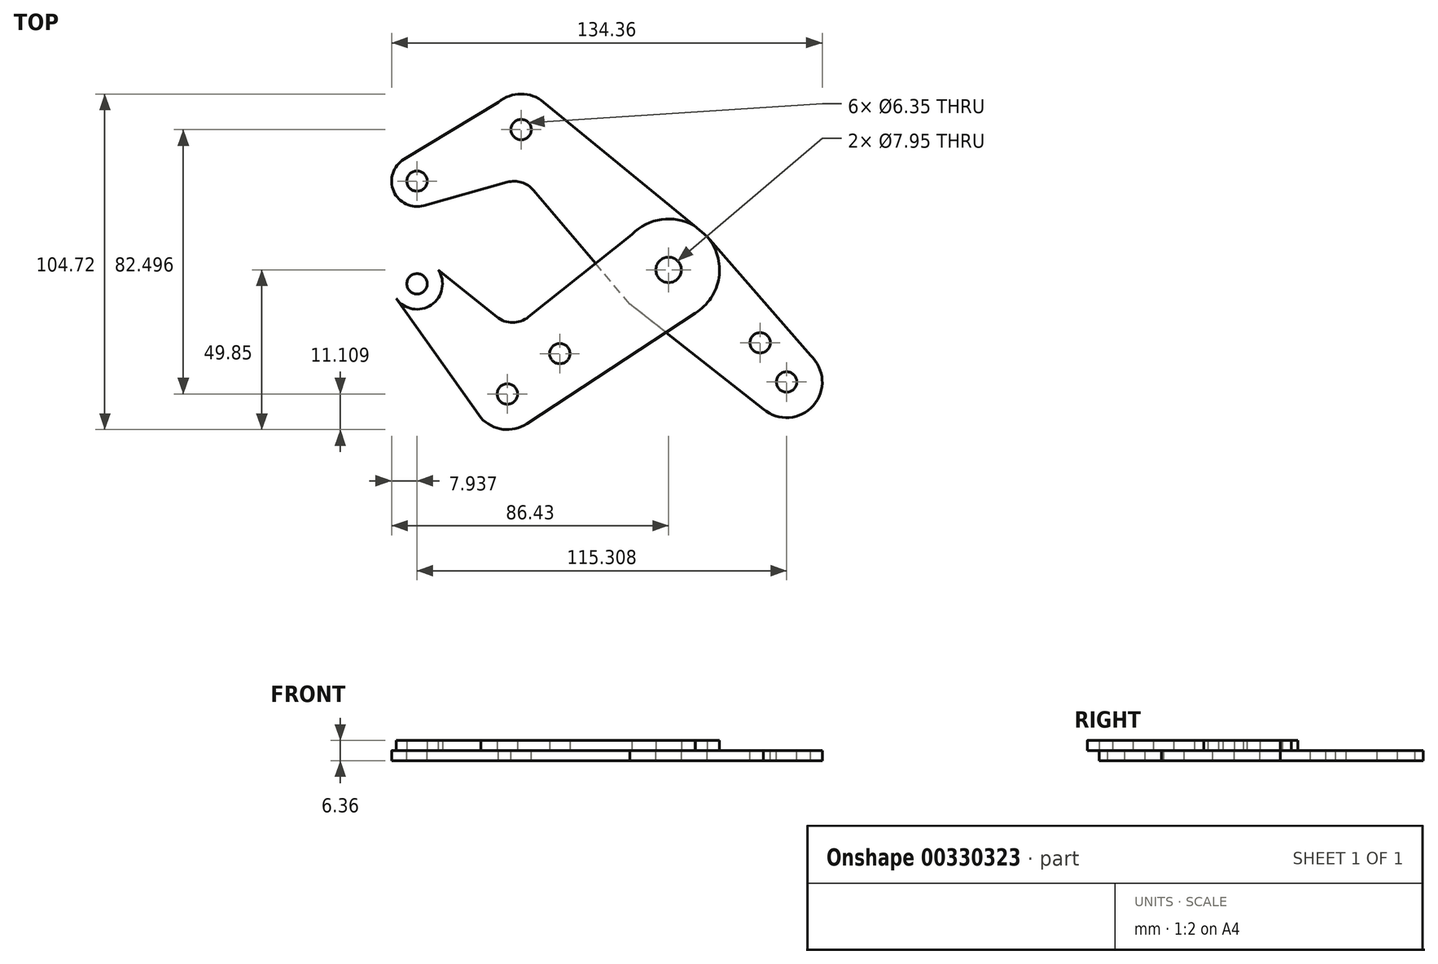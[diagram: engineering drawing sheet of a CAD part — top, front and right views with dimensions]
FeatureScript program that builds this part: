
annotation { "Feature Type Name" : "Feature", "Feature Type Description" : "" }
export const myFeature = defineFeature(function(context is Context, id is Id, definition is map)
    precondition{}
    {
        {
            var Q0;
            Q0=qCreatedBy(makeId("Top.planeOp"),FACE);
            var sketch = newSketch(context, id + "F0", { "sketchPlane" : qUnion([Q0])});
            skCircle(sketch, "E0", {"center": v(0, 0) * mm, "radius": 15.88 * mm});
            skCircle(sketch, "E1", {"center": v(0, 0) * mm, "radius": 3.98 * mm});
            skCircle(sketch, "E2", {"center": v(0, 0) * mm, "radius": 3.18 * mm});
            skLineSegment(sketch, "E3", {"start": v(-89.11, -20.05) * mm, "end": v(-89.92, -20.9) * mm});
            skPoint(sketch, "E4.visualSharp", {"position": v(-56, -35.73) * mm});
            skPoint(sketch, "E5.visualSharp", {"position": v(-95.08, -26.29) * mm});
            skCircle(sketch, "E6", {"center": v(-50.31, -38.74) * mm, "radius": 11.11 * mm});
            skCircle(sketch, "E7", {"center": v(-50.31, -38.74) * mm, "radius": 3.18 * mm});
            skCircle(sketch, "E8", {"center": v(-33.95, -26.14) * mm, "radius": 3.18 * mm});
            skLineSegment(sketch, "E9", {"start": v(8.35, -13.5) * mm, "end": v(-44.21, -48.03) * mm});
            skCircle(sketch, "E10", {"center": v(-78.5, -4.37) * mm, "radius": 7.94 * mm});
            skCircle(sketch, "E11", {"center": v(-78.5, -4.37) * mm, "radius": 3.18 * mm});
            skLineSegment(sketch, "E12", {"start": v(-58.6, -46.15) * mm, "end": v(-84.97, -8.96) * mm});
            skPoint(sketch, "E13.visualSharp", {"position": v(-57.45, -13.47) * mm});
            skCircle(sketch, "E14", {"center": v(36.81, -35) * mm, "radius": 11.11 * mm});
            skCircle(sketch, "E15", {"center": v(36.81, -35) * mm, "radius": 3.18 * mm});
            skCircle(sketch, "E16", {"center": v(28.56, -22.77) * mm, "radius": 3.18 * mm});
            skLineSegment(sketch, "E17", {"start": v(44.23, -26.73) * mm, "end": v(11.99, 10.4) * mm});
            skLineSegment(sketch, "E18", {"start": v(29.58, -43.44) * mm, "end": v(-12.11, -10.67) * mm});
            skCircle(sketch, "E19", {"center": v(-46.02, 43.76) * mm, "radius": 11.11 * mm});
            skCircle(sketch, "E20", {"center": v(-46.02, 43.76) * mm, "radius": 3.18 * mm});
            skCircle(sketch, "E21", {"center": v(-78.5, 27.7) * mm, "radius": 7.94 * mm});
            skCircle(sketch, "E22", {"center": v(-78.5, 27.7) * mm, "radius": 3.18 * mm});
            skLineSegment(sketch, "E23", {"start": v(11.99, 10.4) * mm, "end": v(-38.96, 52.34) * mm});
            skLineSegment(sketch, "E24", {"start": v(-53.08, 52.34) * mm, "end": v(-82.6, 34.5) * mm});
            skPoint(sketch, "E25.visualSharp", {"position": v(-44.52, -22.13) * mm});
            skPoint(sketch, "E26.visualSharp", {"position": v(-50.1, -17.52) * mm});
            skArc(sketch, "E26.filletArc", {"start": v(-50.1, -17.52) * mm, "mid": v(-49.34, -18.07) * mm, "end": v(-48.53, -18.53) * mm});
            skPoint(sketch, "E27.visualSharp", {"position": v(-50.55, 27.7) * mm});
            skLineSegment(sketch, "E28", {"start": v(-12.11, -10.67) * mm, "end": v(-42.14, 24.83) * mm});
            skLineSegment(sketch, "E29", {"start": v(-50.36, 27.35) * mm, "end": v(-76.35, 20.06) * mm});
            skPoint(sketch, "E30.visualSharp", {"position": v(-45.44, 28.74) * mm});
            skArc(sketch, "E30.filletArc", {"start": v(-42.14, 24.83) * mm, "mid": v(-45.88, 27.3) * mm, "end": v(-50.36, 27.35) * mm});
            skLineSegment(sketch, "E31", {"start": v(-11.4, 11.04) * mm, "end": v(-43.7, -14.69) * mm});
            skLineSegment(sketch, "E32", {"start": v(-71.86, 0) * mm, "end": v(-53.65, -14.66) * mm});
            skArc(sketch, "E33.filletArc", {"start": v(-53.65, -14.66) * mm, "mid": v(-48.68, -16.42) * mm, "end": v(-43.7, -14.69) * mm});
            skSolve(sketch);
        }
        {
            var Q0;
            Q0=makeQuery(id+"F0.imprint","IMPRINT",FACE,{"disambiguationData":[TD([[makeQuery(id+"F0.imprint","IMPRINT",EDGE,{"derivedFrom":sQuery(id+"F0.wireOp",EDGE,"E8")}),-1.0]])]});
            var Q1;
            Q1=makeQuery(id+"F0.imprint","IMPRINT",FACE,{"disambiguationData":[TD([[makeQuery(id+"F0.imprint","IMPRINT",EDGE,{"derivedFrom":sQuery(id+"F0.wireOp",EDGE,"E1")}),-1.0]])]});
            var Q2;
            {var subQ0=sQuery(id+"F0.wireOp",EDGE,"E9");var subQ1=sQuery(id+"F0.wireOp",EDGE,"E0");var subQ2=makeQuery(id+"F0.imprint","INTERSECT",VERTEX,{"derivedFrom":[subQ1,subQ0]});Q2=makeQuery(id+"F0.imprint","IMPRINT",FACE,{"disambiguationData":[TD([[makeQuery(id+"F0.imprint","IMPRINT",EDGE,{"disambiguationData":[TD([[subQ2,1.0]])],"derivedFrom":subQ1}),-1.0]])]});}
            var Q3;
            {var subQ0=sQuery(id+"F0.wireOp",EDGE,"E31");var subQ1=sQuery(id+"F0.wireOp",EDGE,"E0");var subQ2=makeQuery(id+"F0.imprint","INTERSECT",VERTEX,{"derivedFrom":[subQ1,subQ0]});Q3=makeQuery(id+"F0.imprint","IMPRINT",FACE,{"disambiguationData":[TD([[makeQuery(id+"F0.imprint","IMPRINT",EDGE,{"disambiguationData":[TD([[subQ2,-1.0]])],"derivedFrom":subQ1}),-1.0]])]});}
            var Q4;
            Q4=makeQuery(id+"F0.imprint","IMPRINT",FACE,{"disambiguationData":[TD([[makeQuery(id+"F0.imprint","IMPRINT",EDGE,{"derivedFrom":sQuery(id+"F0.wireOp",EDGE,"E7")}),-1.0]])]});
            var Q5;
            Q5=makeQuery(id+"F0.imprint","IMPRINT",FACE,{"disambiguationData":[TD([[makeQuery(id+"F0.imprint","IMPRINT",EDGE,{"derivedFrom":sQuery(id+"F0.wireOp",EDGE,"E11")}),1.0]])]});
            extrude(context, id + "F1", {"entities" : qUnion([Q0, Q1, Q2, Q3, Q4, Q5]), "depth" : 3.17 * mm});
        }
        {
            var Q0;
            {var subQ7=sQuery(id+"F0.wireOp",EDGE,"E24");Q0=makeQuery(id+"F0.imprint","IMPRINT",FACE,{"disambiguationData":[TD([[makeQuery(id+"F0.imprint","IMPRINT",EDGE,{"derivedFrom":subQ7}),1.0]])]});}
            var Q1;
            Q1=makeQuery(id+"F0.imprint","IMPRINT",FACE,{"disambiguationData":[TD([[makeQuery(id+"F0.imprint","IMPRINT",EDGE,{"derivedFrom":sQuery(id+"F0.wireOp",EDGE,"E20")}),-1.0]])]});
            var Q2;
            Q2=makeQuery(id+"F0.imprint","IMPRINT",FACE,{"disambiguationData":[TD([[makeQuery(id+"F0.imprint","IMPRINT",EDGE,{"derivedFrom":sQuery(id+"F0.wireOp",EDGE,"E22")}),-1.0]])]});
            var Q3;
            Q3=makeQuery(id+"F0.imprint","IMPRINT",FACE,{"disambiguationData":[TD([[makeQuery(id+"F0.imprint","IMPRINT",EDGE,{"derivedFrom":sQuery(id+"F0.wireOp",EDGE,"E1")}),-1.0]])]});
            var Q4;
            {var subQ0=sQuery(id+"F0.wireOp",EDGE,"E31");var subQ1=sQuery(id+"F0.wireOp",EDGE,"E0");var subQ2=makeQuery(id+"F0.imprint","INTERSECT",VERTEX,{"derivedFrom":[subQ1,subQ0]});Q4=makeQuery(id+"F0.imprint","IMPRINT",FACE,{"disambiguationData":[TD([[makeQuery(id+"F0.imprint","IMPRINT",EDGE,{"disambiguationData":[TD([[subQ2,-1.0]])],"derivedFrom":subQ1}),-1.0]])]});}
            var Q5;
            {var subQ0=sQuery(id+"F0.wireOp",EDGE,"E9");var subQ1=sQuery(id+"F0.wireOp",EDGE,"E0");var subQ2=makeQuery(id+"F0.imprint","INTERSECT",VERTEX,{"derivedFrom":[subQ1,subQ0]});Q5=makeQuery(id+"F0.imprint","IMPRINT",FACE,{"disambiguationData":[TD([[makeQuery(id+"F0.imprint","IMPRINT",EDGE,{"disambiguationData":[TD([[subQ2,1.0]])],"derivedFrom":subQ1}),-1.0]])]});}
            var Q6;
            Q6=makeQuery(id+"F0.imprint","IMPRINT",FACE,{"disambiguationData":[TD([[makeQuery(id+"F0.imprint","IMPRINT",EDGE,{"derivedFrom":sQuery(id+"F0.wireOp",EDGE,"E16")}),-1.0]])]});
            var Q7;
            Q7=makeQuery(id+"F0.imprint","IMPRINT",FACE,{"disambiguationData":[TD([[makeQuery(id+"F0.imprint","IMPRINT",EDGE,{"derivedFrom":sQuery(id+"F0.wireOp",EDGE,"E15")}),-1.0]])]});
            extrude(context, id + "F2", {"entities" : qUnion([Q0, Q1, Q2, Q3, Q4, Q5, Q6, Q7]), "oppositeDirection" : true, "depth" : 3.17 * mm});
        }
    });
